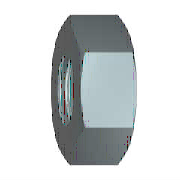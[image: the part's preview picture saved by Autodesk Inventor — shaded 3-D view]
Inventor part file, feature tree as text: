
AUTODESK INVENTOR PART (.ipt)
format: ipt  version: 2022 (Build 260153000, 153)  size: 174,080 bytes
history: native  units: mm (DEFAULTED — no unit token found)
features: sketch x3, other x2, extrude x1, hole x1, plane x1
ambient origin geometry x7: Origin, YZ Plane, XZ Plane, X Axis, Y Axis, Z Axis, Center Point
bodies: Solid1 (feature_tree)
feature tree (8):
  extrude  "Базовый элемент"  Depth=9.237604mm
  other  "Фаска1"
  hole  "Резьба"  [1 undecoded]
  other  "Work Axis1"
  plane  "Work Plane1"
  sketch  "Эскиз1"
  sketch  "Эскиз2"
  sketch  "Эскиз3"
note: 1 required parameter value undecoded (feature->parameter linkage not recoverable at this tier; creation-order binding heuristic only, values carry confidence <= 0.55)
